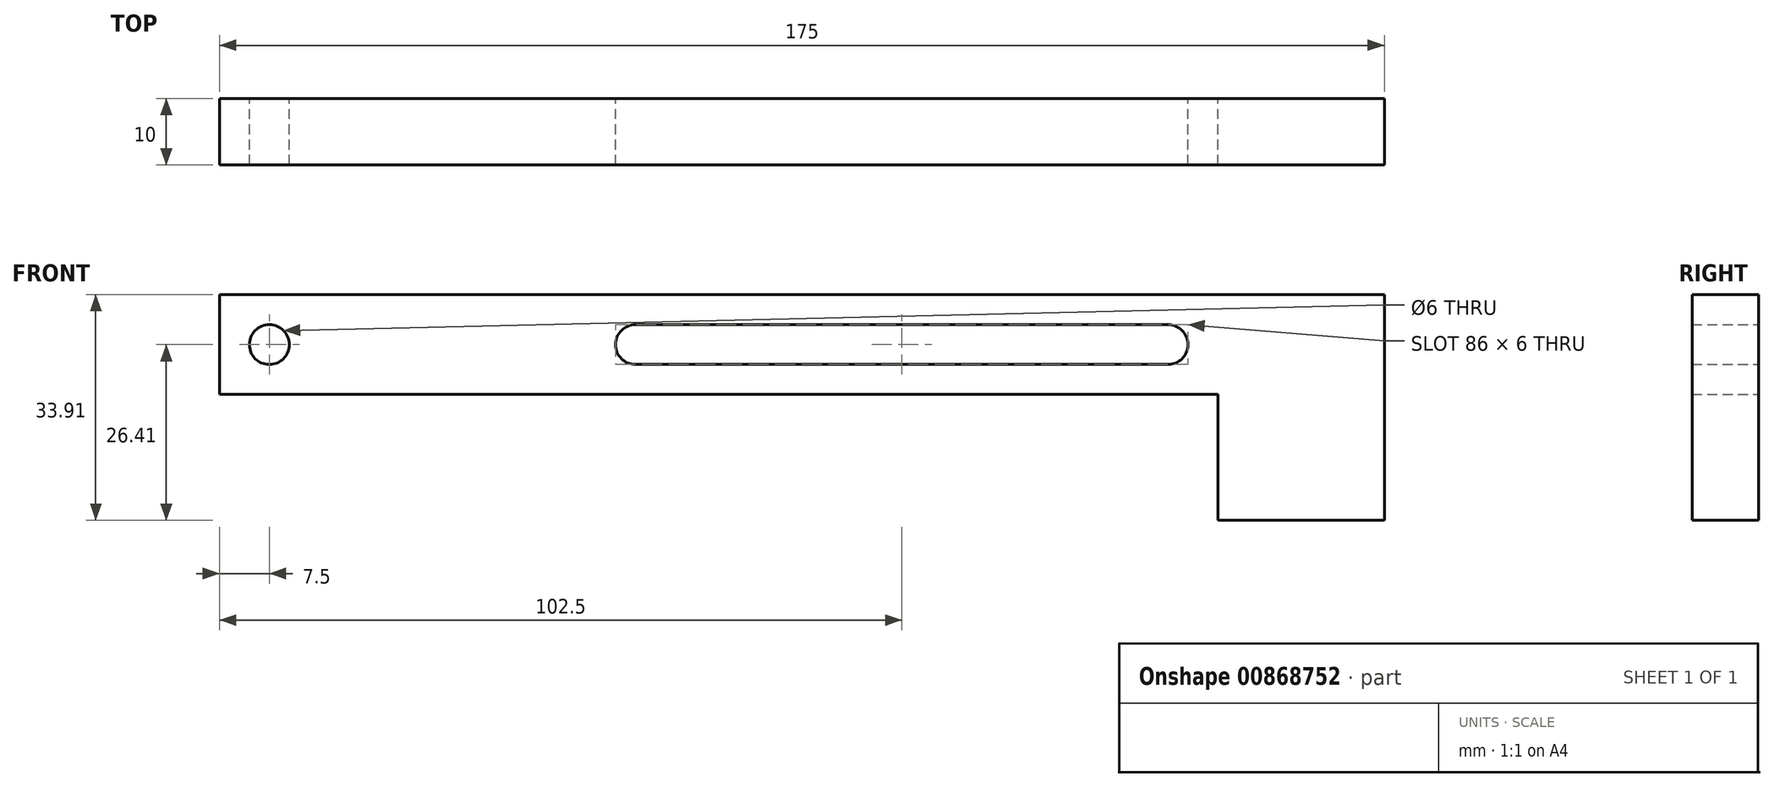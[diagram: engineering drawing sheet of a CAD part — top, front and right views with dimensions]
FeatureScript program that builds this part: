
annotation { "Feature Type Name" : "Feature", "Feature Type Description" : "" }
export const myFeature = defineFeature(function(context is Context, id is Id, definition is map)
    precondition{}
    {
        {
            var Q0;
            Q0=qCreatedBy(makeId("Front.planeOp"),FACE);
            var sketch = newSketch(context, id + "F0", { "sketchPlane" : qUnion([Q0])});
            skCircle(sketch, "E0", {"center": v(0, 0) * mm, "radius": 3 * mm});
            skLineSegment(sketch, "E1.bottom", {"start": v(-7.5, -7.5) * mm, "end": v(142.5, -7.5) * mm});
            skLineSegment(sketch, "E1.top", {"start": v(-7.5, 7.5) * mm, "end": v(142.5, 7.5) * mm});
            skLineSegment(sketch, "E1.left", {"start": v(-7.5, -7.5) * mm, "end": v(-7.5, 7.5) * mm});
            skLineSegment(sketch, "E1.right", {"start": v(142.5, -7.5) * mm, "end": v(142.5, 7.5) * mm});
            skLineSegment(sketch, "E2.bottom", {"start": v(55, 3) * mm, "end": v(135, 3) * mm});
            skLineSegment(sketch, "E2.top", {"start": v(55, -3) * mm, "end": v(135, -3) * mm});
            skArc(sketch, "E3", {"start": v(135, -3) * mm, "mid": v(138, 0) * mm, "end": v(135, 3) * mm});
            skArc(sketch, "E4", {"start": v(55, 3) * mm, "mid": v(52, 0) * mm, "end": v(55, -3) * mm});
            skSolve(sketch);
        }
        {
            var Q0;
            Q0=makeQuery(id+"F0.imprint","IMPRINT",FACE,{"disambiguationData":[TD([[makeQuery(id+"F0.imprint","IMPRINT",EDGE,{"derivedFrom":sQuery(id+"F0.wireOp",EDGE,"E0")}),-1.0]])]});
            extrude(context, id + "F1", {"entities" : qUnion([Q0]), "depth" : 10 * mm, "offsetDistance" : 25 * mm, "symmetric" : true});
        }
        {
            var Q0;
            Q0=qCreatedBy(makeId("Front.planeOp"),FACE);
            var sketch = newSketch(context, id + "F2", { "sketchPlane" : qUnion([Q0])});
            skLineSegment(sketch, "E5.0", {"start": v(142.5, -7.5) * mm, "end": v(142.5, 7.5) * mm});
            skLineSegment(sketch, "E6.bottom", {"start": v(142.5, 7.5) * mm, "end": v(167.5, 7.5) * mm});
            skLineSegment(sketch, "E6.left", {"start": v(142.5, 7.5) * mm, "end": v(142.5, -26.41) * mm});
            skLineSegment(sketch, "E6.right", {"start": v(167.5, 7.5) * mm, "end": v(167.5, -26.41) * mm});
            skLineSegment(sketch, "E7", {"start": v(142.5, -26.41) * mm, "end": v(167.5, -26.41) * mm});
            skPoint(sketch, "E6.top.end.orphan", {"position": v(167.5, -7.5) * mm});
            skSolve(sketch);
        }
        {
            var Q0;
            {var subQ0=sQuery(id+"F2.wireOp",EDGE,"E6.bottom");Q0=makeQuery(id+"F2.imprint","IMPRINT",FACE,{"disambiguationData":[TD([[makeQuery(id+"F2.imprint","IMPRINT",EDGE,{"derivedFrom":subQ0}),-1.0]])]});}
            extrude(context, id + "F3", {"entities" : qUnion([Q0]), "operationType" : NewBodyOperationType.ADD, "depth" : 10 * mm, "offsetDistance" : 25 * mm, "symmetric" : true});
        }
    });
